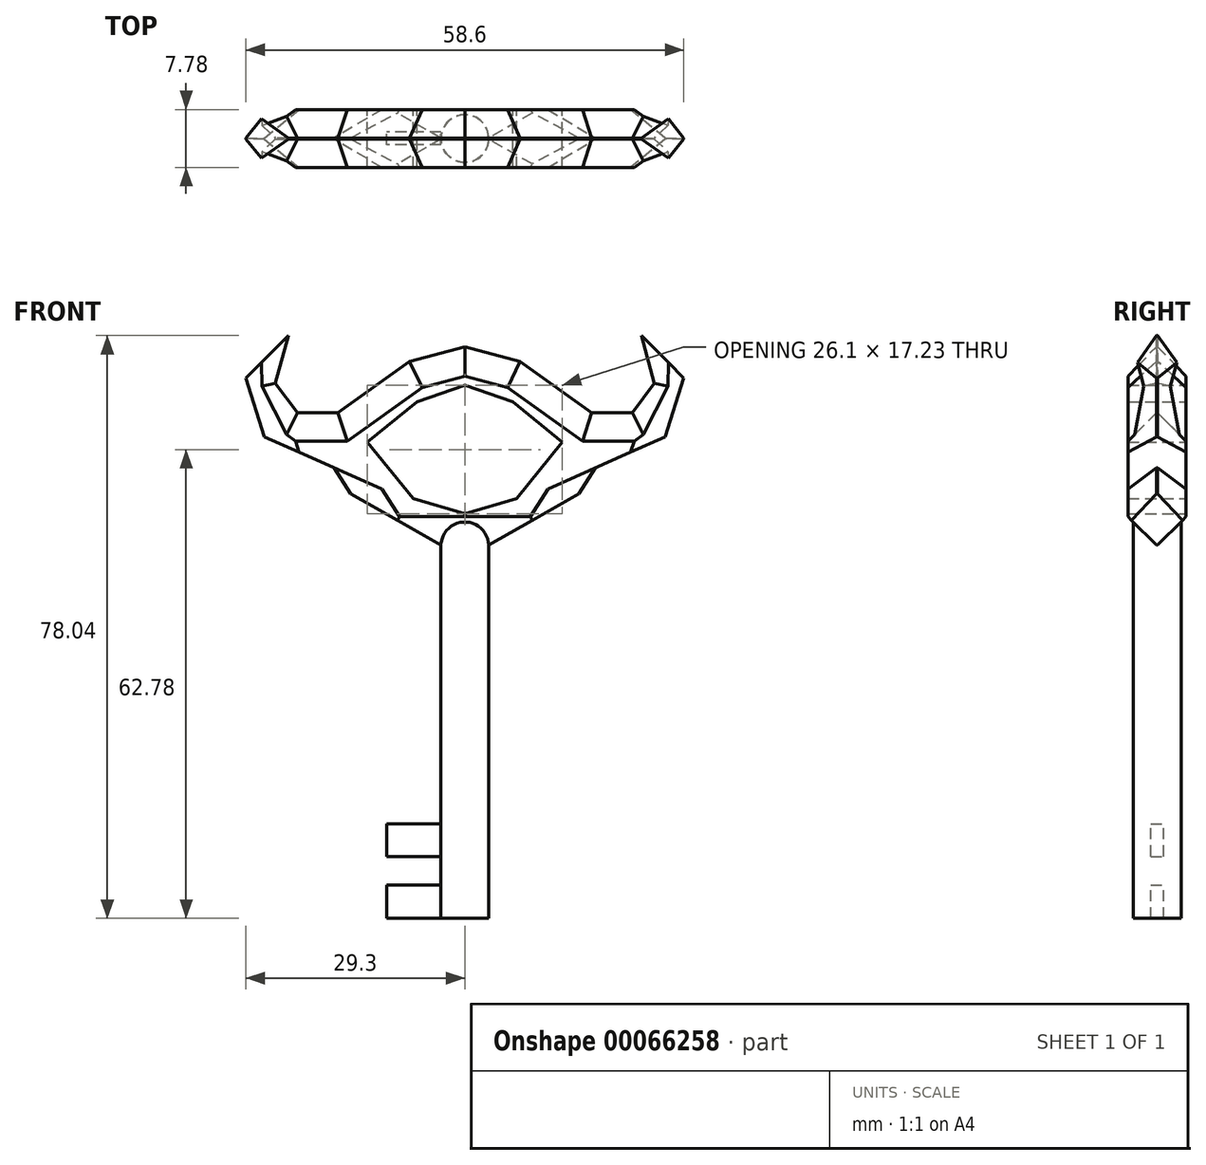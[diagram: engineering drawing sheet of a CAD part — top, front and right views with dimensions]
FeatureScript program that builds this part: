
annotation { "Feature Type Name" : "Feature", "Feature Type Description" : "" }
export const myFeature = defineFeature(function(context is Context, id is Id, definition is map)
    precondition{}
    {
        {
            var Q0;
            Q0=qCreatedBy(makeId("Front.planeOp"),FACE);
            var sketch = newSketch(context, id + "F0", { "sketchPlane" : qUnion([Q0])});
            skLineSegment(sketch, "E0.bottom", {"start": v(0, -33.73) * mm, "end": v(3.2, -33.73) * mm});
            skLineSegment(sketch, "E0.top", {"start": v(0, 16.25) * mm, "end": v(3.2, 16.25) * mm});
            skLineSegment(sketch, "E0.left", {"start": v(0, -33.73) * mm, "end": v(0, 16.25) * mm});
            skLineSegment(sketch, "E0.right", {"start": v(3.2, -33.73) * mm, "end": v(3.2, 16.25) * mm});
            skLineSegment(sketch, "E1.MirrorCS", {"start": v(-3.2, -33.73) * mm, "end": v(-3.2, -29.26) * mm});
            skLineSegment(sketch, "E2.bottom", {"start": v(-3.2, -33.73) * mm, "end": v(-10.46, -33.73) * mm});
            skLineSegment(sketch, "E2.top", {"start": v(-3.2, -29.26) * mm, "end": v(-10.46, -29.26) * mm});
            skLineSegment(sketch, "E2.right", {"start": v(-10.46, -33.73) * mm, "end": v(-10.46, -29.26) * mm});
            skLineSegment(sketch, "E3.bottom", {"start": v(-3.2, -25.43) * mm, "end": v(-10.46, -25.43) * mm});
            skLineSegment(sketch, "E3.top", {"start": v(-3.2, -21.08) * mm, "end": v(-10.46, -21.08) * mm});
            skLineSegment(sketch, "E3.left", {"start": v(-3.2, -25.43) * mm, "end": v(-3.2, -21.08) * mm});
            skLineSegment(sketch, "E3.right", {"start": v(-10.46, -25.43) * mm, "end": v(-10.46, -21.08) * mm});
            skPoint(sketch, "E4.orphan", {"position": v(-3.2, 16.25) * mm});
            skPoint(sketch, "E5.MirrorCS.end.orphan", {"position": v(-3.2, -33.73) * mm});
            skPoint(sketch, "E5.MirrorCS.start.orphan", {"position": v(0, -33.73) * mm});
            skPoint(sketch, "E6.MirrorCS.start.orphan", {"position": v(0, 16.25) * mm});
            skLineSegment(sketch, "E7", {"start": v(3.2, 16.25) * mm, "end": v(15.26, 23.14) * mm});
            skLineSegment(sketch, "E8", {"start": v(15.26, 23.14) * mm, "end": v(17.48, 26.59) * mm});
            skLineSegment(sketch, "E9", {"start": v(17.48, 26.59) * mm, "end": v(26.83, 30.77) * mm});
            skLineSegment(sketch, "E10", {"start": v(26.83, 30.77) * mm, "end": v(29.3, 38.65) * mm});
            skLineSegment(sketch, "E11", {"start": v(29.3, 38.65) * mm, "end": v(23.63, 44.31) * mm});
            skLineSegment(sketch, "E12", {"start": v(23.63, 44.31) * mm, "end": v(25.36, 37.91) * mm});
            skLineSegment(sketch, "E13", {"start": v(25.36, 37.91) * mm, "end": v(22.4, 33.97) * mm});
            skLineSegment(sketch, "E14", {"start": v(22.4, 33.97) * mm, "end": v(16.99, 33.97) * mm});
            skLineSegment(sketch, "E15", {"start": v(16.99, 33.97) * mm, "end": v(7.39, 40.87) * mm});
            skLineSegment(sketch, "E16", {"start": v(7.39, 40.87) * mm, "end": v(0, 42.84) * mm});
            skLineSegment(sketch, "E17", {"start": v(0, 42.84) * mm, "end": v(0, 16.25) * mm});
            skLineSegment(sketch, "E18", {"start": v(0, 37.67) * mm, "end": v(6.4, 35.45) * mm});
            skLineSegment(sketch, "E19", {"start": v(6.4, 35.45) * mm, "end": v(13.05, 30.03) * mm});
            skLineSegment(sketch, "E20", {"start": v(13.05, 30.03) * mm, "end": v(6.9, 22.5) * mm});
            skLineSegment(sketch, "E21", {"start": v(6.9, 22.5) * mm, "end": v(0, 20.43) * mm});
            skLineSegment(sketch, "E22.MirrorCS", {"start": v(-29.3, 38.65) * mm, "end": v(-23.63, 44.31) * mm});
            skLineSegment(sketch, "E23.MirrorCS", {"start": v(-23.63, 44.31) * mm, "end": v(-25.36, 37.91) * mm});
            skLineSegment(sketch, "E24.MirrorCS", {"start": v(-7.39, 40.87) * mm, "end": v(0, 42.84) * mm});
            skLineSegment(sketch, "E25.MirrorCS", {"start": v(-16.99, 33.97) * mm, "end": v(-7.39, 40.87) * mm});
            skLineSegment(sketch, "E26.MirrorCS", {"start": v(-22.4, 33.97) * mm, "end": v(-16.99, 33.97) * mm});
            skLineSegment(sketch, "E27.MirrorCS", {"start": v(-25.36, 37.91) * mm, "end": v(-22.4, 33.97) * mm});
            skLineSegment(sketch, "E28.MirrorCS", {"start": v(-26.83, 30.77) * mm, "end": v(-29.3, 38.65) * mm});
            skLineSegment(sketch, "E29.MirrorCS", {"start": v(-17.48, 26.59) * mm, "end": v(-26.83, 30.77) * mm});
            skLineSegment(sketch, "E30.MirrorCS", {"start": v(-3.2, 16.25) * mm, "end": v(-15.26, 23.14) * mm});
            skLineSegment(sketch, "E31.MirrorCS", {"start": v(-15.26, 23.14) * mm, "end": v(-17.48, 26.59) * mm});
            skLineSegment(sketch, "E32.MirrorCS", {"start": v(-6.9, 22.5) * mm, "end": v(0, 20.43) * mm});
            skLineSegment(sketch, "E33.MirrorCS", {"start": v(-13.05, 30.03) * mm, "end": v(-6.9, 22.5) * mm});
            skLineSegment(sketch, "E34.MirrorCS", {"start": v(-6.4, 35.45) * mm, "end": v(-13.05, 30.03) * mm});
            skLineSegment(sketch, "E35.MirrorCS", {"start": v(0, 37.67) * mm, "end": v(-6.4, 35.45) * mm});
            skLineSegment(sketch, "E36", {"start": v(-3.2, 16.25) * mm, "end": v(0, 16.25) * mm});
            skSolve(sketch);
        }
        {
            var Q0;
            Q0=makeQuery(id+"F0.imprint","IMPRINT",FACE,{"disambiguationData":[TD([[makeQuery(id+"F0.imprint","IMPRINT",EDGE,{"derivedFrom":sQuery(id+"F0.wireOp",EDGE,"E0.bottom")}),1.0]])]});
            var Q1;
            Q1=sQuery(id+"F0.wireOp",EDGE,"E0.left");
            revolve(context, id + "F1", {"entities" : qUnion([Q0]), "axis" : qUnion([Q1]), "revolveType" : RevolveType.FULL});
        }
        {
            var Q0;
            Q0=makeQuery(id+"F0.imprint","IMPRINT",FACE,{"disambiguationData":[TD([[makeQuery(id+"F0.imprint","IMPRINT",EDGE,{"derivedFrom":sQuery(id+"F0.wireOp",EDGE,"E3.bottom")}),-1.0]])]});
            var Q1;
            Q1=makeQuery(id+"F0.imprint","IMPRINT",FACE,{"disambiguationData":[TD([[makeQuery(id+"F0.imprint","IMPRINT",EDGE,{"derivedFrom":sQuery(id+"F0.wireOp",EDGE,"E2.bottom")}),-1.0]])]});
            extrude(context, id + "F2", {"entities" : qUnion([Q0, Q1]), "endBound" : BoundingType.SYMMETRIC, "depth" : 1.7 * mm});
        }
        {
            var Q0;
            {var subQ3=sQuery(id+"F0.wireOp",EDGE,"E0.top");Q0=makeQuery(id+"F0.imprint","IMPRINT",FACE,{"disambiguationData":[TD([[makeQuery(id+"F0.imprint","IMPRINT",EDGE,{"derivedFrom":subQ3}),1.0]])]});}
            var Q1;
            Q1=makeQuery(id+"F0.imprint","IMPRINT",FACE,{"disambiguationData":[TD([[makeQuery(id+"F0.imprint","IMPRINT",EDGE,{"derivedFrom":sQuery(id+"F0.wireOp",EDGE,"E22.MirrorCS")}),-1.0]])]});
            extrude(context, id + "F3", {"entities" : qUnion([Q0, Q1]), "operationType" : NewBodyOperationType.ADD, "endBound" : BoundingType.SYMMETRIC, "depth" : 7.8 * mm});
        }
        {
            var Q0;
            Q0=makeQuery(id+"F3.opExtrude","CAP_EDGE",EDGE,{"disambiguationData":[OSD([sQuery(id+"F0.wireOp",EDGE,"E15")])],"isStart":false});
            var Q1;
            Q1=makeQuery(id+"F3.opExtrude","CAP_EDGE",EDGE,{"disambiguationData":[OSD([sQuery(id+"F0.wireOp",EDGE,"E16")])],"isStart":false});
            var Q2;
            Q2=makeQuery(id+"F3.opExtrude","CAP_EDGE",EDGE,{"disambiguationData":[OSD([sQuery(id+"F0.wireOp",EDGE,"E24.MirrorCS")])],"isStart":false});
            var Q3;
            Q3=makeQuery(id+"F3.opExtrude","CAP_EDGE",EDGE,{"disambiguationData":[OSD([sQuery(id+"F0.wireOp",EDGE,"E25.MirrorCS")])],"isStart":false});
            var Q4;
            Q4=makeQuery(id+"F3.opExtrude","CAP_EDGE",EDGE,{"disambiguationData":[OSD([sQuery(id+"F0.wireOp",EDGE,"E26.MirrorCS")])],"isStart":false});
            var Q5;
            Q5=makeQuery(id+"F3.opExtrude","CAP_EDGE",EDGE,{"disambiguationData":[OSD([sQuery(id+"F0.wireOp",EDGE,"E27.MirrorCS")])],"isStart":false});
            var Q6;
            Q6=makeQuery(id+"F3.opExtrude","CAP_EDGE",EDGE,{"disambiguationData":[OSD([sQuery(id+"F0.wireOp",EDGE,"E23.MirrorCS")])],"isStart":false});
            var Q7;
            Q7=makeQuery(id+"F3.opExtrude","CAP_EDGE",EDGE,{"disambiguationData":[OSD([sQuery(id+"F0.wireOp",EDGE,"E14")])],"isStart":false});
            var Q8;
            Q8=makeQuery(id+"F3.opExtrude","CAP_EDGE",EDGE,{"disambiguationData":[OSD([sQuery(id+"F0.wireOp",EDGE,"E13")])],"isStart":false});
            var Q9;
            Q9=makeQuery(id+"F3.opExtrude","CAP_EDGE",EDGE,{"disambiguationData":[OSD([sQuery(id+"F0.wireOp",EDGE,"E12")])],"isStart":false});
            var Q10;
            Q10=makeQuery(id+"F3.opExtrude","CAP_EDGE",EDGE,{"disambiguationData":[OSD([sQuery(id+"F0.wireOp",EDGE,"E31.MirrorCS")])],"isStart":false});
            var Q11;
            Q11=makeQuery(id+"F3.opExtrude","CAP_EDGE",EDGE,{"disambiguationData":[OSD([sQuery(id+"F0.wireOp",EDGE,"E8")])],"isStart":false});
            var Q12;
            Q12=makeQuery(id+"F3.opExtrude","CAP_EDGE",EDGE,{"disambiguationData":[OSD([sQuery(id+"F0.wireOp",EDGE,"E15")])],"isStart":true});
            var Q13;
            Q13=makeQuery(id+"F3.opExtrude","CAP_EDGE",EDGE,{"disambiguationData":[OSD([sQuery(id+"F0.wireOp",EDGE,"E16")])],"isStart":true});
            var Q14;
            Q14=makeQuery(id+"F3.opExtrude","CAP_EDGE",EDGE,{"disambiguationData":[OSD([sQuery(id+"F0.wireOp",EDGE,"E24.MirrorCS")])],"isStart":true});
            var Q15;
            Q15=makeQuery(id+"F3.opExtrude","CAP_EDGE",EDGE,{"disambiguationData":[OSD([sQuery(id+"F0.wireOp",EDGE,"E25.MirrorCS")])],"isStart":true});
            var Q16;
            Q16=makeQuery(id+"F3.opExtrude","CAP_EDGE",EDGE,{"disambiguationData":[OSD([sQuery(id+"F0.wireOp",EDGE,"E26.MirrorCS")])],"isStart":true});
            var Q17;
            Q17=makeQuery(id+"F3.opExtrude","CAP_EDGE",EDGE,{"disambiguationData":[OSD([sQuery(id+"F0.wireOp",EDGE,"E27.MirrorCS")])],"isStart":true});
            var Q18;
            Q18=makeQuery(id+"F3.opExtrude","CAP_EDGE",EDGE,{"disambiguationData":[OSD([sQuery(id+"F0.wireOp",EDGE,"E23.MirrorCS")])],"isStart":true});
            var Q19;
            Q19=makeQuery(id+"F3.opExtrude","CAP_EDGE",EDGE,{"disambiguationData":[OSD([sQuery(id+"F0.wireOp",EDGE,"E14")])],"isStart":true});
            var Q20;
            Q20=makeQuery(id+"F3.opExtrude","CAP_EDGE",EDGE,{"disambiguationData":[OSD([sQuery(id+"F0.wireOp",EDGE,"E13")])],"isStart":true});
            var Q21;
            Q21=makeQuery(id+"F3.opExtrude","CAP_EDGE",EDGE,{"disambiguationData":[OSD([sQuery(id+"F0.wireOp",EDGE,"E12")])],"isStart":true});
            var Q22;
            Q22=makeQuery(id+"F3.opExtrude","CAP_EDGE",EDGE,{"disambiguationData":[OSD([sQuery(id+"F0.wireOp",EDGE,"E8")])],"isStart":true});
            var Q23;
            Q23=makeQuery(id+"F3.opExtrude","CAP_EDGE",EDGE,{"disambiguationData":[OSD([sQuery(id+"F0.wireOp",EDGE,"E31.MirrorCS")])],"isStart":true});
            var Q24;
            Q24=makeQuery(id+"F3.opExtrude","CAP_EDGE",EDGE,{"disambiguationData":[OSD([sQuery(id+"F0.wireOp",EDGE,"E10")])],"isStart":true});
            var Q25;
            Q25=makeQuery(id+"F3.opExtrude","CAP_EDGE",EDGE,{"disambiguationData":[OSD([sQuery(id+"F0.wireOp",EDGE,"E10")])],"isStart":false});
            var Q26;
            Q26=makeQuery(id+"F3.opExtrude","CAP_EDGE",EDGE,{"disambiguationData":[OSD([sQuery(id+"F0.wireOp",EDGE,"E28.MirrorCS")])],"isStart":false});
            var Q27;
            Q27=makeQuery(id+"F3.opExtrude","CAP_EDGE",EDGE,{"disambiguationData":[OSD([sQuery(id+"F0.wireOp",EDGE,"E28.MirrorCS")])],"isStart":true});
            var Q28;
            Q28=makeQuery(id+"F3.opExtrude","CAP_EDGE",EDGE,{"disambiguationData":[OSD([sQuery(id+"F0.wireOp",EDGE,"E0.top"),sQuery(id+"F0.wireOp",EDGE,"E36")])],"isStart":false});
            var Q29;
            Q29=makeQuery(id+"F3.opExtrude","CAP_EDGE",EDGE,{"disambiguationData":[OSD([sQuery(id+"F0.wireOp",EDGE,"E0.top"),sQuery(id+"F0.wireOp",EDGE,"E36")])],"isStart":true});
            chamfer(context, id + "F4", {"entities" : qUnion([Q0, Q1, Q2, Q3, Q4, Q5, Q6, Q7, Q8, Q9, Q10, Q11, Q12, Q13, Q14, Q15, Q16, Q17, Q18, Q19, Q20, Q21, Q22, Q23, Q24, Q25, Q26, Q27, Q28, Q29]), "width" : 3.8 * mm, "tangentPropagation" : true});
        }
    });
